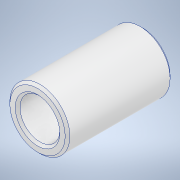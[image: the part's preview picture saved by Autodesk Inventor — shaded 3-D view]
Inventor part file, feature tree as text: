
AUTODESK INVENTOR PART (.ipt)
format: ipt  version: 2020 (Build 240168000, 168)  size: 116,224 bytes
history: native  units: mm
features: extrude x1, chamfer x1, sketch x1
ambient origin geometry x8: Origin, YZ Plane, XZ Plane, XY Plane, X Axis, Y Axis, Z Axis, Center Point
bodies: Solid1 (feature_tree)
feature tree (3):
  extrude  "Extrusion1"  Depth=11.1125mm
  chamfer  "Chamfer1"  Distance=11.1125mm
  sketch  "Sketch1"  dims[d0=6.35mm d1=4.2164mm d2=11.1125mm d3=0.0mm d4=0.25mm d5=2.0mm d6=45.0deg]
